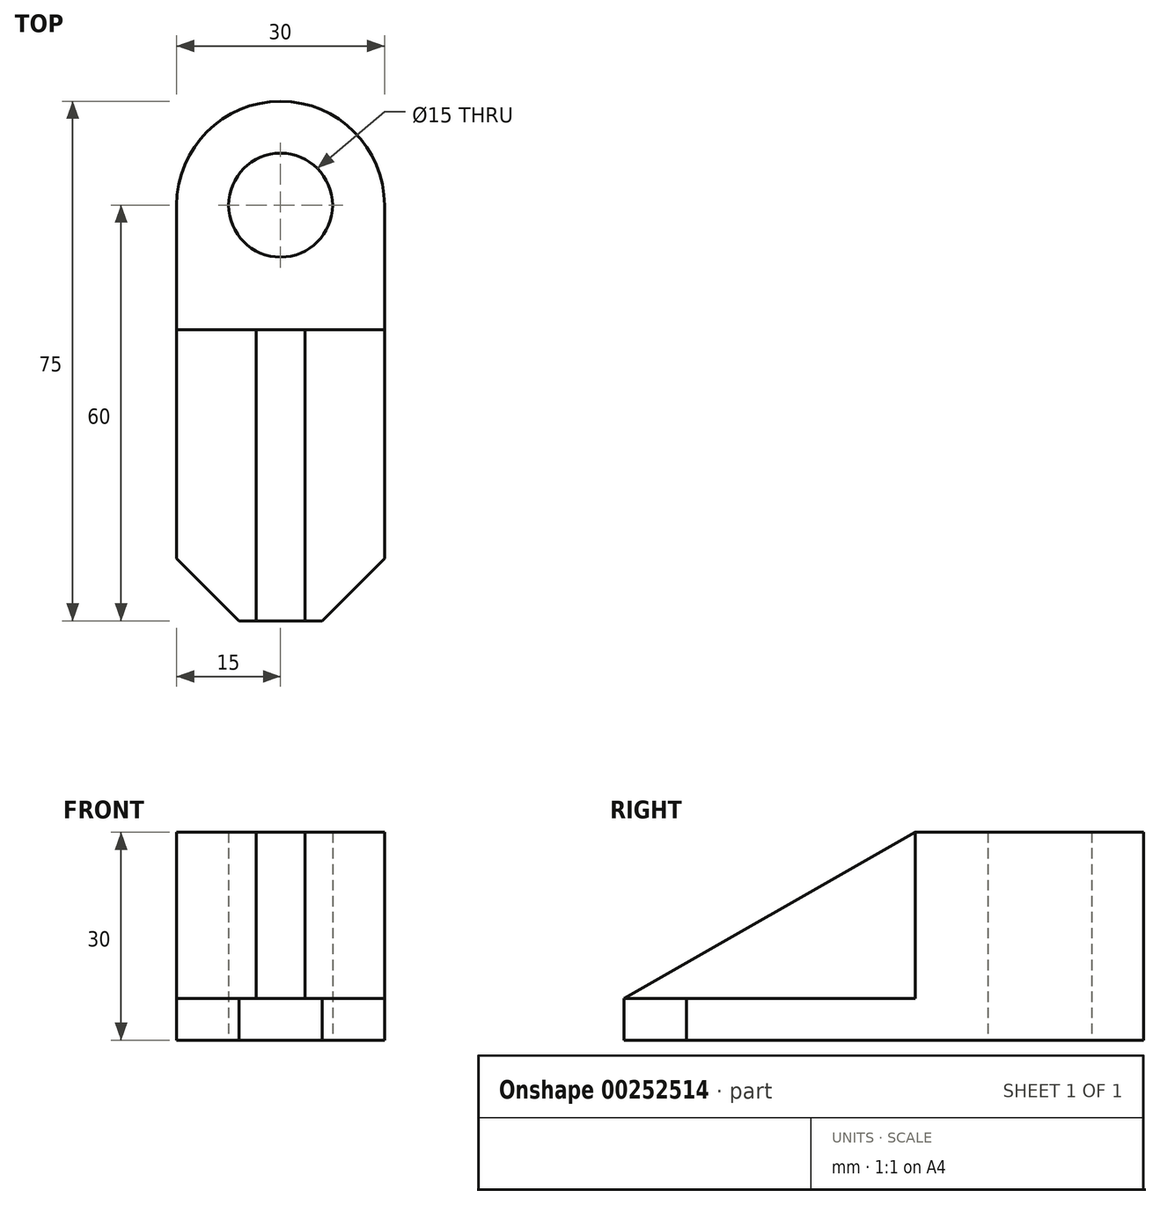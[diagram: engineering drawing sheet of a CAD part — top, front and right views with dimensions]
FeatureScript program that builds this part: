
annotation { "Feature Type Name" : "Feature", "Feature Type Description" : "" }
export const myFeature = defineFeature(function(context is Context, id is Id, definition is map)
    precondition{}
    {
        {
            var Q0;
            Q0=qCreatedBy(makeId("Top.planeOp"),FACE);
            var sketch = newSketch(context, id + "F0", { "sketchPlane" : qUnion([Q0])});
            skArc(sketch, "E0", {"start": v(15, 0) * mm, "mid": v(0, 15) * mm, "end": v(-15, 0) * mm});
            skLineSegment(sketch, "E1", {"start": v(-15, 0) * mm, "end": v(-15, -18) * mm});
            skLineSegment(sketch, "E2", {"start": v(15, 0) * mm, "end": v(15, -18) * mm});
            skLineSegment(sketch, "E3", {"start": v(-15, -18) * mm, "end": v(15, -18) * mm});
            skCircle(sketch, "E4", {"center": v(0, 0) * mm, "radius": 7.5 * mm});
            skLineSegment(sketch, "E5", {"start": v(-15, -18) * mm, "end": v(-15, -60) * mm});
            skLineSegment(sketch, "E6", {"start": v(15, -18) * mm, "end": v(15, -60) * mm});
            skLineSegment(sketch, "E7", {"start": v(-15, -60) * mm, "end": v(15, -60) * mm});
            skLineSegment(sketch, "E8", {"start": v(0, -18) * mm, "end": v(0, -60) * mm, "construction": true});
            skLineSegment(sketch, "E9", {"start": v(-3.5, -18) * mm, "end": v(-3.5, -60) * mm});
            skLineSegment(sketch, "E10.MirrorCS", {"start": v(3.5, -18) * mm, "end": v(3.5, -60) * mm});
            skLineSegment(sketch, "E11", {"start": v(6, -60) * mm, "end": v(15, -51) * mm});
            skLineSegment(sketch, "E12.MirrorCS", {"start": v(-6, -60) * mm, "end": v(-15, -51) * mm});
            skSolve(sketch);
        }
        {
            var Q0;
            Q0=makeQuery(id+"F0.imprint","IMPRINT",FACE,{"disambiguationData":[TD([[makeQuery(id+"F0.imprint","IMPRINT",EDGE,{"derivedFrom":sQuery(id+"F0.wireOp",EDGE,"E0")}),1.0]])]});
            extrude(context, id + "F1", {"entities" : qUnion([Q0]), "depth" : 30 * mm});
        }
        {
            var Q0;
            {var subQ0=sQuery(id+"F0.wireOp",EDGE,"E10.MirrorCS");Q0=makeQuery(id+"F0.imprint","IMPRINT",FACE,{"disambiguationData":[TD([[makeQuery(id+"F0.imprint","IMPRINT",EDGE,{"derivedFrom":subQ0}),1.0]])]});}
            var Q1;
            {var subQ0=sQuery(id+"F0.wireOp",EDGE,"E9");Q1=makeQuery(id+"F0.imprint","IMPRINT",FACE,{"disambiguationData":[TD([[makeQuery(id+"F0.imprint","IMPRINT",EDGE,{"derivedFrom":subQ0}),1.0]])]});}
            var Q2;
            {var subQ0=sQuery(id+"F0.wireOp",EDGE,"E9");Q2=makeQuery(id+"F0.imprint","IMPRINT",FACE,{"disambiguationData":[TD([[makeQuery(id+"F0.imprint","IMPRINT",EDGE,{"derivedFrom":subQ0}),-1.0]])]});}
            extrude(context, id + "F2", {"entities" : qUnion([Q0, Q1, Q2]), "operationType" : NewBodyOperationType.ADD, "depth" : 6 * mm});
        }
        {
            var Q0;
            Q0=makeQuery(id+"F2.opExtrude","CAP_FACE",FACE,{"disambiguationData":[OSD([sQuery(id+"F0.wireOp",EDGE,"E3"),sQuery(id+"F0.wireOp",EDGE,"E5"),sQuery(id+"F0.wireOp",EDGE,"E6"),sQuery(id+"F0.wireOp",EDGE,"E7"),sQuery(id+"F0.wireOp",EDGE,"E11"),sQuery(id+"F0.wireOp",EDGE,"E12.MirrorCS")])],"isStart":false});
            var sketch = newSketch(context, id + "F3", { "sketchPlane" : qUnion([Q0])});
            skLineSegment(sketch, "E13.0", {"start": v(-3.5, -18) * mm, "end": v(-3.5, -60) * mm});
            skLineSegment(sketch, "E14.0", {"start": v(3.5, -18) * mm, "end": v(3.5, -60) * mm});
            skLineSegment(sketch, "E15", {"start": v(-3.5, -18) * mm, "end": v(3.5, -18) * mm});
            skLineSegment(sketch, "E16", {"start": v(-3.5, -60) * mm, "end": v(3.5, -60) * mm});
            skSolve(sketch);
        }
        {
            var Q0;
            Q0=makeQuery(id+"F3.imprint","IMPRINT",FACE,{"disambiguationData":[TD([[makeQuery(id+"F3.imprint","IMPRINT",EDGE,{"derivedFrom":sQuery(id+"F3.wireOp",EDGE,"E13.0")}),1.0]])]});
            extrude(context, id + "F4", {"entities" : qUnion([Q0]), "operationType" : NewBodyOperationType.ADD, "depth" : 24 * mm});
        }
        {
            var Q0;
            Q0=makeQuery(id+"F4.opExtrude","SWEPT_FACE",FACE,{"disambiguationData":[OSD([sQuery(id+"F3.wireOp",EDGE,"E14.0")])]});
            var sketch = newSketch(context, id + "F5", { "sketchPlane" : qUnion([Q0])});
            skLineSegment(sketch, "E17", {"start": v(-60, 6) * mm, "end": v(-18, 30) * mm});
            skSolve(sketch);
        }
        {
            var Q0;
            Q0=makeQuery(id+"F5.imprint","IMPRINT",FACE,{"disambiguationData":[TD([[makeQuery(id+"F5.imprint","IMPRINT",EDGE,{"derivedFrom":sQuery(id+"F5.wireOp",EDGE,"E17")}),1.0]])]});
            extrude(context, id + "F6", {"entities" : qUnion([Q0]), "operationType" : NewBodyOperationType.REMOVE, "endBound" : BoundingType.THROUGH_ALL, "oppositeDirection" : true, "depth" : 25.4 * mm});
        }
    });
